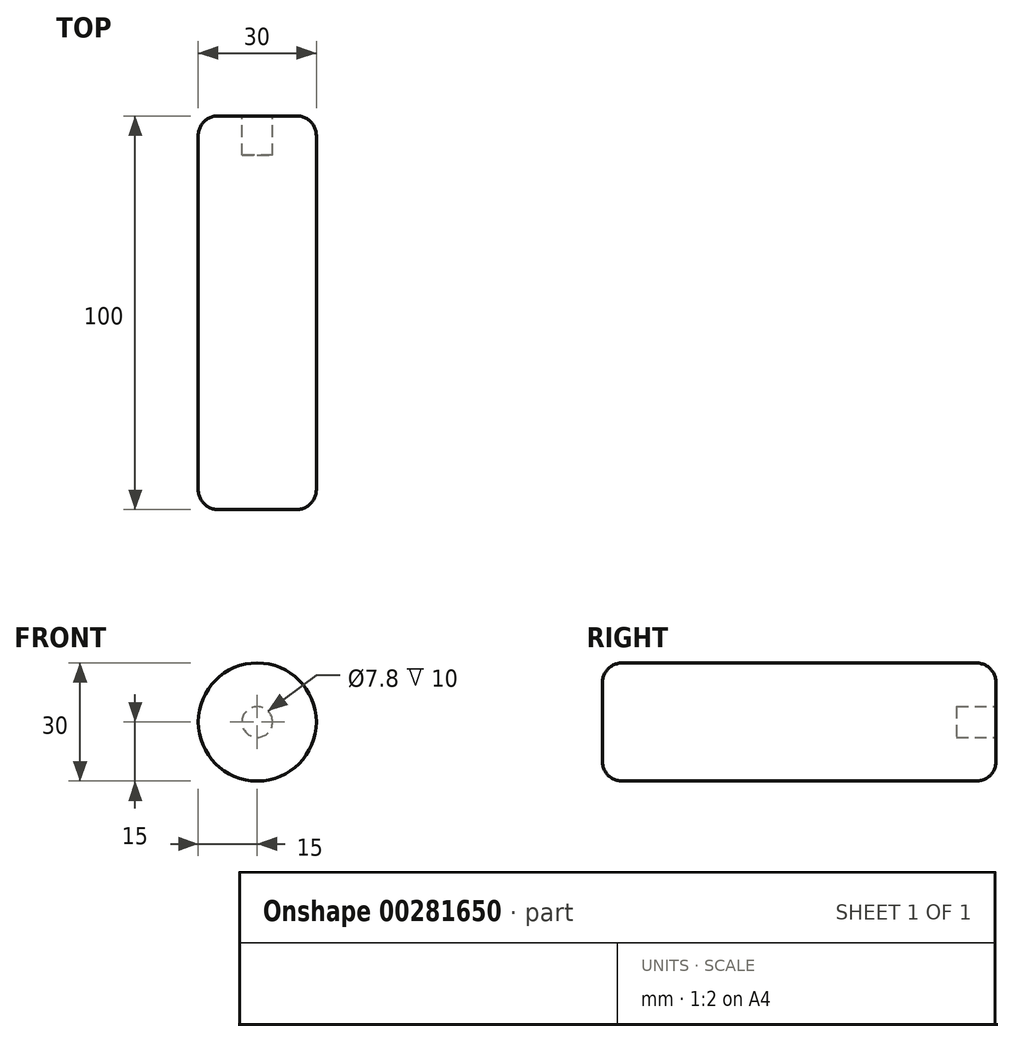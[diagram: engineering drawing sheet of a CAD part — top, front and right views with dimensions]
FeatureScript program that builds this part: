
annotation { "Feature Type Name" : "Feature", "Feature Type Description" : "" }
export const myFeature = defineFeature(function(context is Context, id is Id, definition is map)
    precondition{}
    {
        {
            var Q0;
            Q0=qCreatedBy(makeId("Top.planeOp"),FACE);
            var sketch = newSketch(context, id + "F0", { "sketchPlane" : qUnion([Q0])});
            skLineSegment(sketch, "E0", {"start": v(0, 0) * mm, "end": v(-15, 0) * mm});
            skLineSegment(sketch, "E1", {"start": v(-15, 0) * mm, "end": v(-15, -100) * mm});
            skLineSegment(sketch, "E2", {"start": v(-15, -100) * mm, "end": v(0, -100) * mm});
            skLineSegment(sketch, "E3", {"start": v(0, -100) * mm, "end": v(0, 0) * mm});
            skSolve(sketch);
        }
        {
            var Q0;
            Q0=makeQuery(id+"F0.imprint","IMPRINT",FACE,{"disambiguationData":[TD([[makeQuery(id+"F0.imprint","IMPRINT",EDGE,{"derivedFrom":sQuery(id+"F0.wireOp",EDGE,"E0")}),1.0]])]});
            var Q1;
            Q1=sQuery(id+"F0.wireOp",EDGE,"E3");
            revolve(context, id + "F1", {"entities" : qUnion([Q0]), "axis" : qUnion([Q1]), "revolveType" : RevolveType.FULL});
        }
        {
            var Q0;
            Q0=makeQuery(id+"F1.opRevolve","SWEPT_FACE",FACE,{"disambiguationData":[OSD([sQuery(id+"F0.wireOp",EDGE,"E0")])]});
            var sketch = newSketch(context, id + "F2", { "sketchPlane" : qUnion([Q0])});
            skCircle(sketch, "E4", {"center": v(0, 0) * mm, "radius": 3.9 * mm});
            skSolve(sketch);
        }
        {
            var Q0;
            Q0=makeQuery(id+"F2.imprint","IMPRINT",FACE,{"disambiguationData":[TD([[makeQuery(id+"F2.imprint","IMPRINT",EDGE,{"derivedFrom":sQuery(id+"F2.wireOp",EDGE,"E4")}),1.0]])]});
            extrude(context, id + "F3", {"entities" : qUnion([Q0]), "operationType" : NewBodyOperationType.REMOVE, "oppositeDirection" : true, "depth" : 10 * mm});
        }
        {
            var Q0;
            Q0=makeQuery(id+"F1.opRevolve","SWEPT_EDGE",EDGE,{"disambiguationData":[OSD([sQuery(id+"F0.wireOp",EDGE,"E0"),sQuery(id+"F0.wireOp",EDGE,"E1")])]});
            var Q1;
            Q1=makeQuery(id+"F1.opRevolve","SWEPT_EDGE",EDGE,{"disambiguationData":[OSD([sQuery(id+"F0.wireOp",EDGE,"E1"),sQuery(id+"F0.wireOp",EDGE,"E2")])]});
            fillet(context, id + "F4", {"entities" : qUnion([Q0, Q1]), "radius" : 5 * mm, "tangentPropagation" : true});
        }
    });
